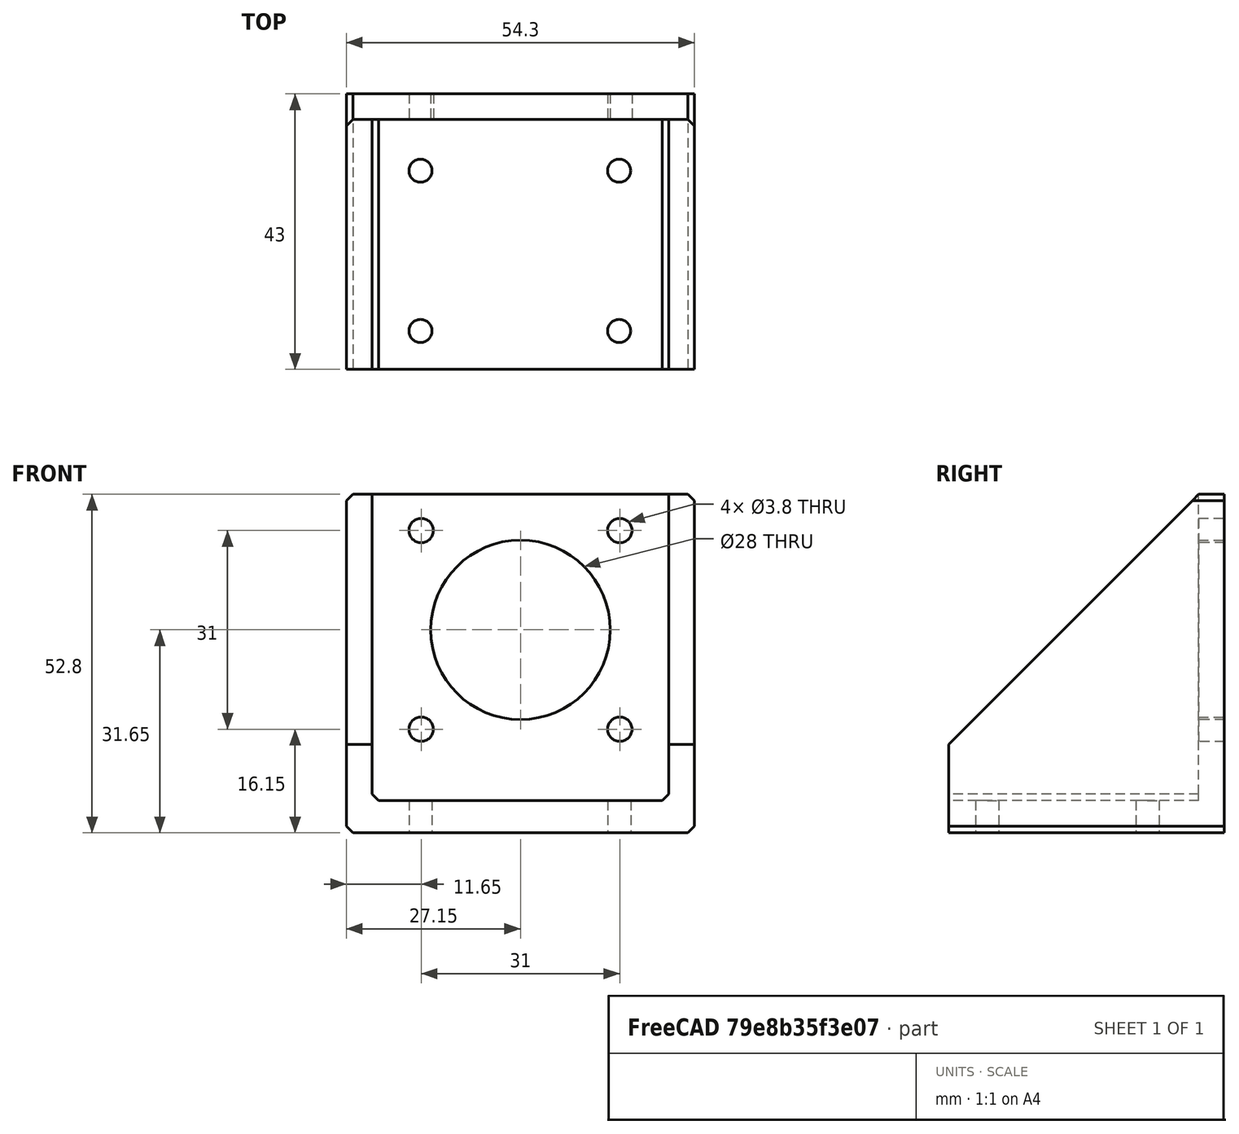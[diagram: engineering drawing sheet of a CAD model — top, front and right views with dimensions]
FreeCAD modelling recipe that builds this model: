
FCSTD DOCUMENT  (FreeCAD 0.16R6706 (Git))
Label: Nema holder 3.0
License: All rights reserved
LicenseURL: http://en.wikipedia.org/wiki/All_rights_reserved
objects: Part::Cylinder×4, Part::Cut×4, Part::Feature×1
note: 9 computed .brp shape members not serialized (recipe doc carries the construction recipe); baked Part::Feature solids carry a one-line shape summary decoded from their .brp

FEATURE [Part::Cylinder] Cylinder008  label="Cilindro002"
  Angle = 360
  Height = 40
  Placement = pos=(34.5,31,-11) rot=(0,0,1;0rad)
  Radius = 1.8
FEATURE [Part::Cylinder] Cylinder009  label="Cilindro003"
  Angle = 360
  Height = 40
  Placement = pos=(65.5,31,-11) rot=(0,0,1;0rad)
  Radius = 1.8
FEATURE [Part::Cylinder] Cylinder006  label="Cilindro"
  Angle = 360
  Height = 40
  Placement = pos=(34.5,6,-11) rot=(0,0,1;0rad)
  Radius = 1.8
FEATURE [Part::Cylinder] Cylinder007  label="Cilindro001"
  Angle = 360
  Height = 40
  Placement = pos=(65.5,6,-11) rot=(0,0,1;0rad)
  Radius = 1.8
FEATURE [Part::Feature] nema_holder
  Placement = pos=(49.9,39,-32) rot=(0.57735,0.57735,-0.57735;2.0944rad)
  shape: bbox 54.3 x 43 x 52.8 mm, 27 faces (baked)
FEATURE [Part::Cut] Cut010035003002
  Base = -> nema_holder
  Tool = -> Cylinder006
FEATURE [Part::Cut] Cut010035003003
  Base = -> Cut010035003002
  Tool = -> Cylinder007
FEATURE [Part::Cut] Cut010035003004
  Base = -> Cut010035003003
  Tool = -> Cylinder009
FEATURE [Part::Cut] Cut010035003005  label="nema holder modificados taladros"
  Base = -> Cut010035003004
  Placement = pos=(100,0,8) rot=(0,1,0;3.14159rad)
  Tool = -> Cylinder008
